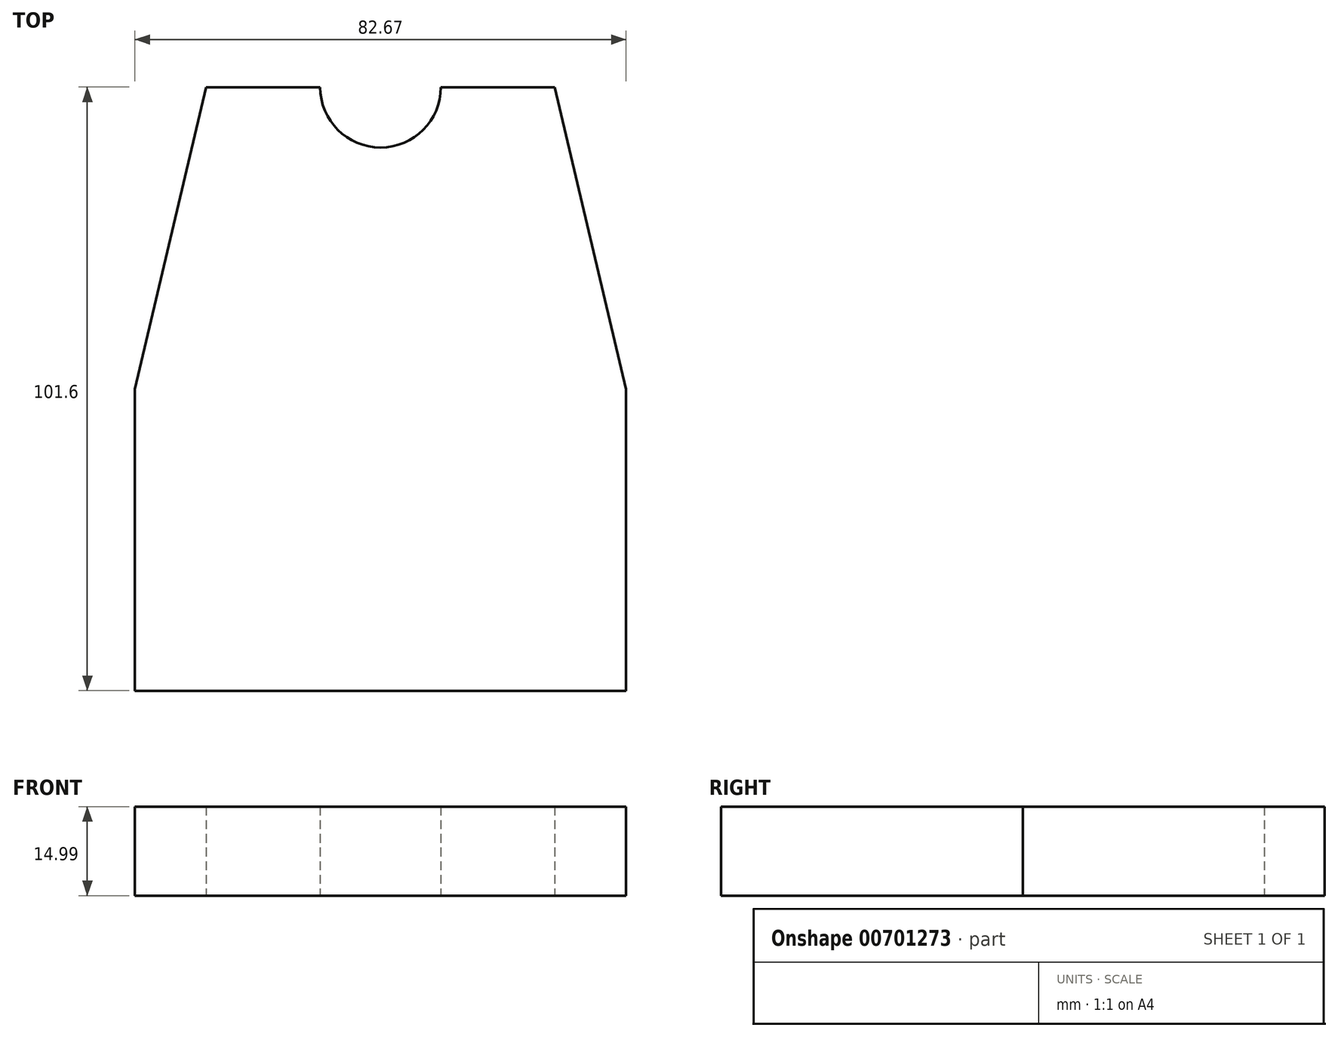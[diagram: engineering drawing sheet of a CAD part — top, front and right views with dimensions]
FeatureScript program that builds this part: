
annotation { "Feature Type Name" : "Feature", "Feature Type Description" : "" }
export const myFeature = defineFeature(function(context is Context, id is Id, definition is map)
    precondition{}
    {
        {
            var Q0;
            Q0=qCreatedBy(makeId("Top.planeOp"),FACE);
            var sketch = newSketch(context, id + "F0", { "sketchPlane" : qUnion([Q0])});
            skLineSegment(sketch, "E0", {"start": v(-33.86, -33.1) * mm, "end": v(-33.86, 17.7) * mm});
            skLineSegment(sketch, "E1", {"start": v(-33.86, 17.7) * mm, "end": v(-21.85, 68.5) * mm});
            skLineSegment(sketch, "E2", {"start": v(-21.85, 68.5) * mm, "end": v(36.8, 68.5) * mm});
            skLineSegment(sketch, "E3", {"start": v(36.8, 68.5) * mm, "end": v(48.8, 17.7) * mm});
            skLineSegment(sketch, "E4", {"start": v(48.8, 17.7) * mm, "end": v(48.8, -33.1) * mm});
            skLineSegment(sketch, "E5", {"start": v(48.8, -33.1) * mm, "end": v(-33.86, -33.1) * mm});
            skCircle(sketch, "E6", {"center": v(7.48, 68.5) * mm, "radius": 10.16 * mm});
            skSolve(sketch);
        }
        {
            var Q0;
            Q0=makeQuery(id+"F0.imprint","IMPRINT",FACE,{"disambiguationData":[TD([[makeQuery(id+"F0.imprint","IMPRINT",EDGE,{"derivedFrom":sQuery(id+"F0.wireOp",EDGE,"E0")}),-1.0]])]});
            var Q1;
            {var subQ0=sQuery(id+"F0.wireOp",EDGE,"E6");var subQ1=sQuery(id+"F0.wireOp",EDGE,"E2");var subQ2=makeQuery(id+"F0.imprint","INTERSECT",VERTEX,{"disambiguationData":[OD(0.0)],"derivedFrom":[subQ1,subQ0]});Q1=makeQuery(id+"F0.imprint","IMPRINT",FACE,{"disambiguationData":[TD([[makeQuery(id+"F0.imprint","IMPRINT",EDGE,{"disambiguationData":[TD([[subQ2,-1.0]])],"derivedFrom":subQ1}),-1.0]])]});}
            var Q2;
            {var subQ0=sQuery(id+"F0.wireOp",EDGE,"E6");var subQ1=sQuery(id+"F0.wireOp",EDGE,"E2");var subQ2=makeQuery(id+"F0.imprint","INTERSECT",VERTEX,{"disambiguationData":[OD(0.0)],"derivedFrom":[subQ1,subQ0]});Q2=makeQuery(id+"F0.imprint","IMPRINT",FACE,{"disambiguationData":[TD([[makeQuery(id+"F0.imprint","IMPRINT",EDGE,{"disambiguationData":[TD([[subQ2,-1.0]])],"derivedFrom":subQ1}),1.0]])]});}
            extrude(context, id + "F1", {"entities" : qUnion([Q0, Q1, Q2]), "depth" : 15 * mm, "offsetDistance" : 25.4 * mm});
        }
    });
